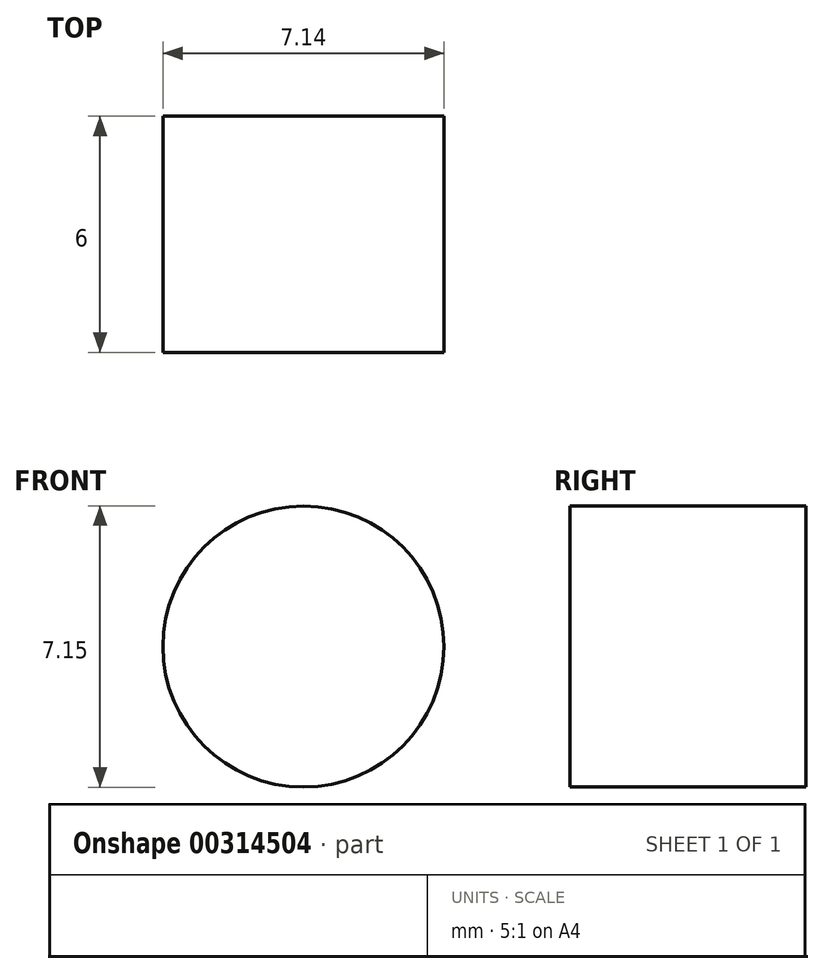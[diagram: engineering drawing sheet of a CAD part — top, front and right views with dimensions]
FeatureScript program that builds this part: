
annotation { "Feature Type Name" : "Feature", "Feature Type Description" : "" }
export const myFeature = defineFeature(function(context is Context, id is Id, definition is map)
    precondition{}
    {
        {
            var Q0;
            Q0=qCreatedBy(makeId("Front.planeOp"),FACE);
            var sketch = newSketch(context, id + "F0", { "sketchPlane" : qUnion([Q0])});
            skCircle(sketch, "E0", {"center": v(15, -31.23) * mm, "radius": 3.57 * mm});
            skCircle(sketch, "E1", {"center": v(-15, -31.23) * mm, "radius": 3.57 * mm});
            skCircle(sketch, "E2", {"center": v(15, 0.27) * mm, "radius": 2.52 * mm});
            skCircle(sketch, "E3", {"center": v(-15, 0.27) * mm, "radius": 2.52 * mm});
            skLineSegment(sketch, "E4", {"start": v(22.26, -18.83) * mm, "end": v(22.26, -12.12) * mm});
            skLineSegment(sketch, "E5", {"start": v(19.76, -18.83) * mm, "end": v(19.76, -12.12) * mm});
            skLineSegment(sketch, "E6", {"start": v(-19.75, -18.83) * mm, "end": v(-19.75, -12.12) * mm});
            skLineSegment(sketch, "E7", {"start": v(-22.25, -18.83) * mm, "end": v(-22.25, -12.12) * mm});
            skLineSegment(sketch, "E8", {"start": v(18.83, 59.52) * mm, "end": v(-18.83, 59.52) * mm});
            skLineSegment(sketch, "E9", {"start": v(25, -34.3) * mm, "end": v(25, 50.7) * mm});
            skArc(sketch, "E10", {"start": v(18.83, -40.48) * mm, "mid": v(23.2, -38.67) * mm, "end": v(25, -34.3) * mm});
            skLineSegment(sketch, "E11", {"start": v(-18.83, -40.48) * mm, "end": v(18.83, -40.48) * mm});
            skLineSegment(sketch, "E12", {"start": v(-25, -34.3) * mm, "end": v(-25, 50.7) * mm});
            skArc(sketch, "E13", {"start": v(-25, -34.3) * mm, "mid": v(-23.2, -38.67) * mm, "end": v(-18.83, -40.48) * mm});
            skCircle(sketch, "E14", {"center": v(0, -30.48) * mm, "radius": 1.3 * mm});
            skCircle(sketch, "E15", {"center": v(0, -10.48) * mm, "radius": 1.3 * mm});
            skCircle(sketch, "E16", {"center": v(0, 9.52) * mm, "radius": 1.3 * mm});
            skCircle(sketch, "E17", {"center": v(0, 29.52) * mm, "radius": 2.55 * mm});
            skCircle(sketch, "E18", {"center": v(0, 49.52) * mm, "radius": 1.3 * mm});
            skLineSegment(sketch, "E19", {"start": v(-25, 50.7) * mm, "end": v(-25, 54.52) * mm});
            skLineSegment(sketch, "E20", {"start": v(-20, 59.52) * mm, "end": v(-18.83, 59.52) * mm});
            skLineSegment(sketch, "E21", {"start": v(18.83, 59.52) * mm, "end": v(20, 59.52) * mm});
            skLineSegment(sketch, "E22", {"start": v(25, 54.52) * mm, "end": v(25, 50.7) * mm});
            skPoint(sketch, "E23.visualSharp", {"position": v(-25, 59.52) * mm});
            skArc(sketch, "E23.filletArc", {"start": v(-20, 59.52) * mm, "mid": v(-23.54, 58.06) * mm, "end": v(-25, 54.52) * mm});
            skPoint(sketch, "E24.visualSharp", {"position": v(25, 59.52) * mm});
            skArc(sketch, "E24.filletArc", {"start": v(25, 54.52) * mm, "mid": v(23.54, 58.06) * mm, "end": v(20, 59.52) * mm});
            skArc(sketch, "E25", {"start": v(-19.75, -12.12) * mm, "mid": v(-21, -10.87) * mm, "end": v(-22.25, -12.12) * mm});
            skArc(sketch, "E26", {"start": v(-22.25, -18.83) * mm, "mid": v(-21, -20.08) * mm, "end": v(-19.75, -18.83) * mm});
            skArc(sketch, "E27", {"start": v(22.26, -12.12) * mm, "mid": v(21, -10.88) * mm, "end": v(19.76, -12.12) * mm});
            skArc(sketch, "E28", {"start": v(19.76, -18.83) * mm, "mid": v(21, -20.08) * mm, "end": v(22.26, -18.83) * mm});
            skLineSegment(sketch, "E29", {"start": v(19.76, -15.48) * mm, "end": v(-19.75, -15.48) * mm, "construction": true});
            skSolve(sketch);
        }
        {
            var Q0;
            Q0=makeQuery(id+"F0.imprint","IMPRINT",FACE,{"disambiguationData":[TD([[makeQuery(id+"F0.imprint","IMPRINT",EDGE,{"derivedFrom":sQuery(id+"F0.wireOp",EDGE,"E0")}),1.0]])]});
            extrude(context, id + "F1", {"entities" : qUnion([Q0]), "depth" : 6 * mm});
        }
    });
